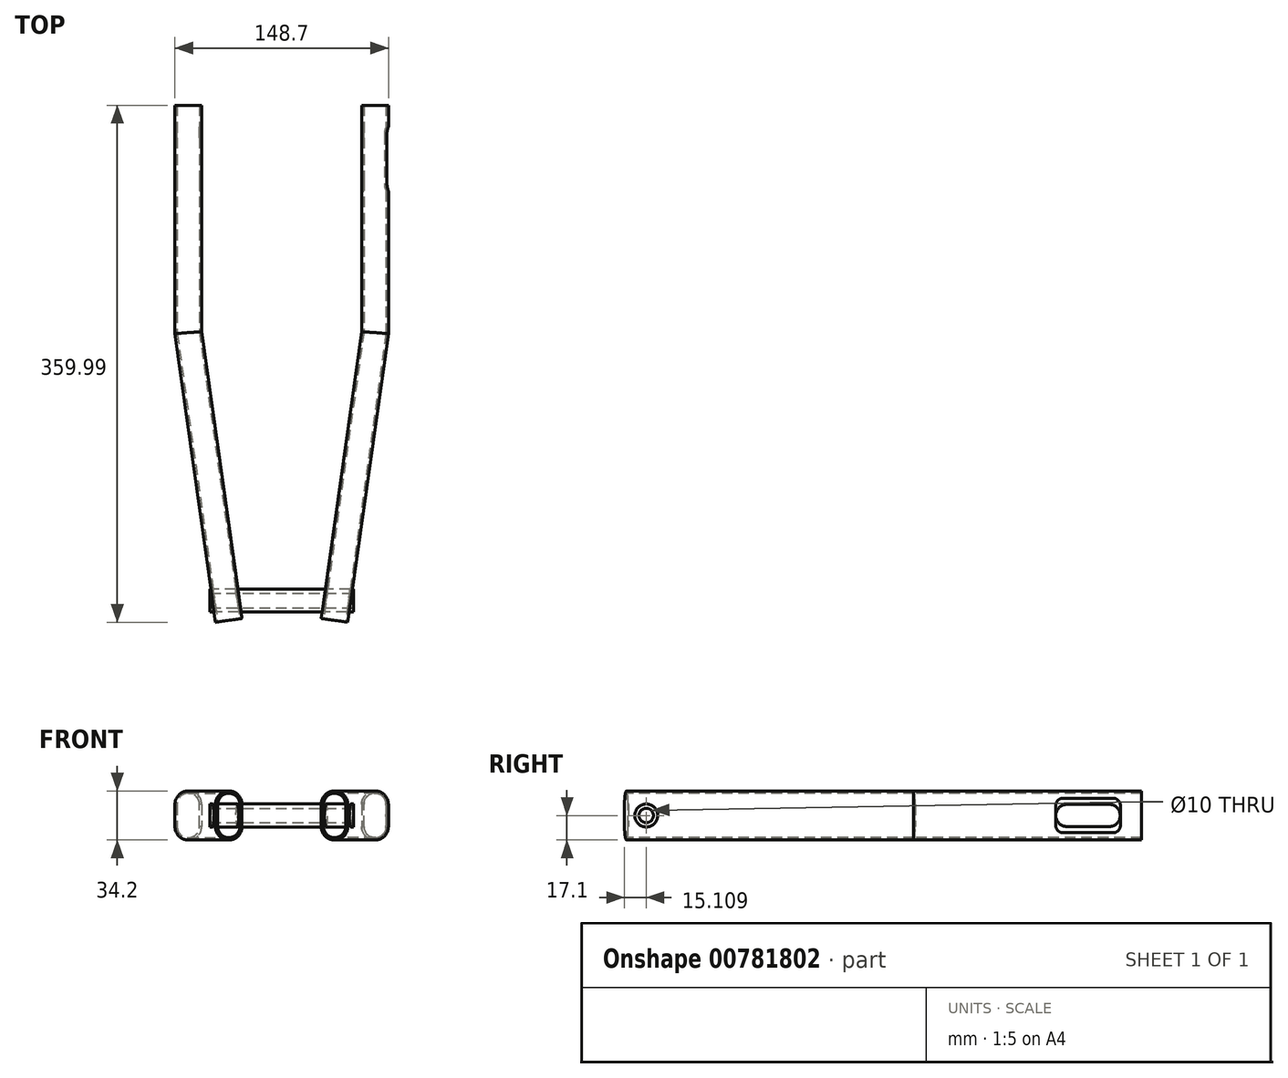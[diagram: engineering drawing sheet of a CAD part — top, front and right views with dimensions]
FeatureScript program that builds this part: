
annotation { "Feature Type Name" : "Feature", "Feature Type Description" : "" }
export const myFeature = defineFeature(function(context is Context, id is Id, definition is map)
    precondition{}
    {
        {
            var Q0;
            Q0=qCreatedBy(makeId("Front.planeOp"),FACE);
            var sketch = newSketch(context, id + "F0", { "sketchPlane" : qUnion([Q0])});
            skLineSegment(sketch, "E0.left", {"start": v(-57.25, -7.75) * mm, "end": v(-57.25, 7.75) * mm});
            skLineSegment(sketch, "E0.right", {"start": v(-72.75, -7.75) * mm, "end": v(-72.75, 7.75) * mm});
            skPoint(sketch, "E0.middle", {"position": v(-65, 0) * mm});
            skArc(sketch, "E1", {"start": v(-57.25, 7.75) * mm, "mid": v(-65, 15.5) * mm, "end": v(-72.75, 7.75) * mm});
            skArc(sketch, "E2", {"start": v(-72.75, -7.75) * mm, "mid": v(-65, -15.5) * mm, "end": v(-57.25, -7.75) * mm});
            skLineSegment(sketch, "E3", {"start": v(-74.35, 7.75) * mm, "end": v(-74.35, -7.75) * mm});
            skLineSegment(sketch, "E4", {"start": v(-55.65, 7.75) * mm, "end": v(-55.65, -7.75) * mm});
            skArc(sketch, "E5", {"start": v(-55.65, 7.75) * mm, "mid": v(-65, 17.1) * mm, "end": v(-74.35, 7.75) * mm});
            skArc(sketch, "E6", {"start": v(-74.35, -7.75) * mm, "mid": v(-65, -17.1) * mm, "end": v(-55.65, -7.75) * mm});
            skLineSegment(sketch, "E7", {"start": v(-65, 0) * mm, "end": v(0, 0) * mm});
            skSolve(sketch);
        }
        {
            var Q0;
            Q0=qCreatedBy(makeId("Top.planeOp"),FACE);
            var sketch = newSketch(context, id + "F1", { "sketchPlane" : qUnion([Q0])});
            skPoint(sketch, "E8.start.orphan", {"position": v(-65, 0) * mm});
            skLineSegment(sketch, "E9", {"start": v(-65, 0) * mm, "end": v(-65, -158.3) * mm});
            skLineSegment(sketch, "E10", {"start": v(-65, -158.3) * mm, "end": v(-36.84, -358.7) * mm});
            skSolve(sketch);
        }
        {
            var Q0;
            Q0 = qSketchRegion(id + "F0", true);
            var Q1;
            Q1=sQuery(id+"F1.wireOp",EDGE,"E9");
            var Q2;
            Q2=sQuery(id+"F1.wireOp",EDGE,"E10");
            sweep(context, id + "F2", {"profiles" : qUnion([Q0]), "path" : qUnion([Q1, Q2])});
        }
        {
            var Q0;
            Q0=makeQuery(id+"F2.opSweep","SWEPT_BODY",BODY,{"disambiguationData":[OSD([sQuery(id+"F0.wireOp",EDGE,"E0.left"),sQuery(id+"F0.wireOp",EDGE,"E0.right"),sQuery(id+"F0.wireOp",EDGE,"E1"),sQuery(id+"F0.wireOp",EDGE,"E2"),sQuery(id+"F0.wireOp",EDGE,"E3"),sQuery(id+"F0.wireOp",EDGE,"E4"),sQuery(id+"F0.wireOp",EDGE,"E5"),sQuery(id+"F0.wireOp",EDGE,"E6"),sQuery(id+"F1.wireOp",EDGE,"E10")])]});
            var Q1;
            Q1=qCreatedBy(makeId("Right.planeOp"),FACE);
            mirror(context, id + "F3", {"operationType" : NewBodyOperationType.ADD, "entities" : qUnion([Q0]), "mirrorPlane" : qUnion([Q1])});
        }
        {
            var Q0;
            Q0=makeQuery(id+"F3.opPattern","COPY",FACE,{"derivedFrom":makeQuery(id+"F2.opSweep","SWEPT_FACE",FACE,{"disambiguationData":[OSD([sQuery(id+"F0.wireOp",EDGE,"E3"),sQuery(id+"F1.wireOp",EDGE,"E9")])]}),"instanceName":"1"});
            var sketch = newSketch(context, id + "F4", { "sketchPlane" : qUnion([Q0])});
            skLineSegment(sketch, "E11.bottom", {"start": v(-22.54, -7.75) * mm, "end": v(-52.04, -7.75) * mm});
            skLineSegment(sketch, "E11.top", {"start": v(-22.54, 7.75) * mm, "end": v(-52.04, 7.75) * mm});
            skPoint(sketch, "E11.middle", {"position": v(-37.3, 0) * mm});
            skArc(sketch, "E12", {"start": v(-22.54, -7.75) * mm, "mid": v(-14.79, 0) * mm, "end": v(-22.54, 7.75) * mm});
            skArc(sketch, "E13", {"start": v(-52.04, 7.75) * mm, "mid": v(-59.8, 0) * mm, "end": v(-52.04, -7.75) * mm});
            skSolve(sketch);
        }
        {
            var Q0;
            Q0 = qSketchRegion(id + "F4", true);
            extrude(context, id + "F5", {"entities" : qUnion([Q0]), "operationType" : NewBodyOperationType.REMOVE, "oppositeDirection" : true, "depth" : 25 * mm, "offsetDistance" : 25 * mm});
        }
        {
            var Q0;
            Q0=makeQuery(id+"F2.opSweep","SWEPT_FACE",FACE,{"disambiguationData":[OSD([sQuery(id+"F0.wireOp",EDGE,"E3"),sQuery(id+"F1.wireOp",EDGE,"E9")])]});
            var sketch = newSketch(context, id + "F6", { "sketchPlane" : qUnion([Q0])});
            skLineSegment(sketch, "E14.bottom", {"start": v(52.04, -7.75) * mm, "end": v(22.54, -7.75) * mm});
            skLineSegment(sketch, "E14.top", {"start": v(52.04, 7.75) * mm, "end": v(22.54, 7.75) * mm});
            skPoint(sketch, "E14.middle", {"position": v(37.3, 0) * mm});
            skArc(sketch, "E15", {"start": v(52.04, -7.75) * mm, "mid": v(59.8, 0) * mm, "end": v(52.04, 7.75) * mm});
            skArc(sketch, "E16", {"start": v(22.54, 7.75) * mm, "mid": v(14.79, 0) * mm, "end": v(22.54, -7.75) * mm});
            skSolve(sketch);
        }
        {
            var Q0;
            Q0 = qSketchRegion(id + "F6", true);
            extrude(context, id + "F7", {"entities" : qUnion([Q0]), "operationType" : NewBodyOperationType.REMOVE, "oppositeDirection" : true, "depth" : 25 * mm, "offsetDistance" : 25 * mm});
        }
        {
            var Q0;
            {var subQ2=sQuery(id+"F1.wireOp",EDGE,"E9");var subQ4=sQuery(id+"F0.wireOp",EDGE,"E3");Q0=makeQuery(id+"F5.boolean.opBoolean","SPLIT",FACE,{"disambiguationData":[TD([makeQuery(id+"F5.opExtrude","SWEPT_FACE",FACE,{"disambiguationData":[OSD([sQuery(id+"F4.wireOp",EDGE,"E13")])]})])],"derivedFrom":makeQuery(id+"F3.opPattern","COPY",FACE,{"derivedFrom":makeQuery(id+"F2.opSweep","SWEPT_FACE",FACE,{"disambiguationData":[OSD([subQ4,subQ2])]}),"instanceName":"1"})});}
            cPlane(context, id + "F8", {"entities" : qUnion([Q0]), "cplaneType" : CPlaneType.OFFSET, "offset" : 25 * mm, "width" : 150 * mm, "height" : 150 * mm});
        }
        {
            var Q0;
            Q0=qCreatedBy(id+"F8.planeOp",FACE);
            var sketch = newSketch(context, id + "F9", { "sketchPlane" : qUnion([Q0])});
            skLineSegment(sketch, "E17.bottom", {"start": v(-19.76, -12) * mm, "end": v(-54.76, -12) * mm});
            skLineSegment(sketch, "E17.top", {"start": v(-19.76, 12) * mm, "end": v(-54.76, 12) * mm});
            skLineSegment(sketch, "E17.left", {"start": v(-14.76, -7) * mm, "end": v(-14.76, 7) * mm});
            skLineSegment(sketch, "E17.right", {"start": v(-59.76, -7) * mm, "end": v(-59.76, 7) * mm});
            skPoint(sketch, "E17.middle", {"position": v(-37.26, 0) * mm});
            skPoint(sketch, "E18.visualSharp", {"position": v(-59.76, 12) * mm});
            skArc(sketch, "E18.filletArc", {"start": v(-54.76, 12) * mm, "mid": v(-58.3, 10.54) * mm, "end": v(-59.76, 7) * mm});
            skPoint(sketch, "E19.visualSharp", {"position": v(-14.76, 12) * mm});
            skArc(sketch, "E19.filletArc", {"start": v(-14.76, 7) * mm, "mid": v(-16.22, 10.54) * mm, "end": v(-19.76, 12) * mm});
            skPoint(sketch, "E20.visualSharp", {"position": v(-14.76, -12) * mm});
            skArc(sketch, "E20.filletArc", {"start": v(-19.76, -12) * mm, "mid": v(-16.22, -10.54) * mm, "end": v(-14.76, -7) * mm});
            skPoint(sketch, "E21.visualSharp", {"position": v(-59.76, -12) * mm});
            skArc(sketch, "E21.filletArc", {"start": v(-59.76, -7) * mm, "mid": v(-58.3, -10.54) * mm, "end": v(-54.76, -12) * mm});
            skSolve(sketch);
        }
        {
            var Q0;
            Q0 = qSketchRegion(id + "F9", true);
            extrude(context, id + "F10", {"entities" : qUnion([Q0]), "operationType" : NewBodyOperationType.REMOVE, "oppositeDirection" : true, "depth" : 30 * mm, "offsetDistance" : 25 * mm});
        }
        {
            var Q0;
            Q0=makeQuery(id+"F3.opPattern","COPY",BODY,{"derivedFrom":makeQuery(id+"F2.opSweep","SWEPT_BODY",BODY,{"disambiguationData":[OSD([sQuery(id+"F0.wireOp",EDGE,"E0.left"),sQuery(id+"F0.wireOp",EDGE,"E0.right"),sQuery(id+"F0.wireOp",EDGE,"E1"),sQuery(id+"F0.wireOp",EDGE,"E2"),sQuery(id+"F0.wireOp",EDGE,"E3"),sQuery(id+"F0.wireOp",EDGE,"E4"),sQuery(id+"F0.wireOp",EDGE,"E5"),sQuery(id+"F0.wireOp",EDGE,"E6"),sQuery(id+"F1.wireOp",EDGE,"E10")])]}),"instanceName":"1"});
            var Q1;
            Q1=qCreatedBy(makeId("Right.planeOp"),FACE);
            mirror(context, id + "F11", {"operationType" : NewBodyOperationType.ADD, "entities" : qUnion([Q0]), "mirrorPlane" : qUnion([Q1])});
        }
        {
            var Q0;
            Q0=makeQuery(id+"F3.opPattern","COPY",BODY,{"derivedFrom":makeQuery(id+"F2.opSweep","SWEPT_BODY",BODY,{"disambiguationData":[OSD([sQuery(id+"F0.wireOp",EDGE,"E0.left"),sQuery(id+"F0.wireOp",EDGE,"E0.right"),sQuery(id+"F0.wireOp",EDGE,"E1"),sQuery(id+"F0.wireOp",EDGE,"E2"),sQuery(id+"F0.wireOp",EDGE,"E3"),sQuery(id+"F0.wireOp",EDGE,"E4"),sQuery(id+"F0.wireOp",EDGE,"E5"),sQuery(id+"F0.wireOp",EDGE,"E6"),sQuery(id+"F1.wireOp",EDGE,"E10")])]}),"instanceName":"1"});
            var Q1;
            Q1=qCreatedBy(makeId("Right.planeOp"),FACE);
            mirror(context, id + "F12", {"entities" : qUnion([Q0]), "mirrorPlane" : qUnion([Q1])});
        }
        {
            var Q0;
            Q0=qCreatedBy(makeId("Right.planeOp"),FACE);
            var sketch = newSketch(context, id + "F13", { "sketchPlane" : qUnion([Q0])});
            skCircle(sketch, "E22", {"center": v(-344.88, 0) * mm, "radius": 8 * mm});
            skSolve(sketch);
        }
        {
            var Q0;
            Q0=makeQuery(id+"F13.imprint","IMPRINT",FACE,{"disambiguationData":[TD([[makeQuery(id+"F13.imprint","IMPRINT",EDGE,{"derivedFrom":sQuery(id+"F13.wireOp",EDGE,"E22")}),1.0]])]});
            extrude(context, id + "F14", {"entities" : qUnion([Q0]), "operationType" : NewBodyOperationType.ADD, "endBound" : BoundingType.SYMMETRIC, "depth" : 100 * mm, "offsetDistance" : 25 * mm});
        }
        {
            var Q0;
            Q0=makeQuery(id+"F14.opExtrude","CAP_FACE",FACE,{"disambiguationData":[OSD([sQuery(id+"F13.wireOp",EDGE,"E22")])],"isStart":false});
            var sketch = newSketch(context, id + "F15", { "sketchPlane" : qUnion([Q0])});
            skCircle(sketch, "E23", {"center": v(-344.88, 0) * mm, "radius": 5 * mm});
            skSolve(sketch);
        }
        {
            var Q0;
            Q0=makeQuery(id+"F15.imprint","IMPRINT",FACE,{"disambiguationData":[TD([[makeQuery(id+"F15.imprint","IMPRINT",EDGE,{"derivedFrom":sQuery(id+"F15.wireOp",EDGE,"E23")}),1.0]])]});
            extrude(context, id + "F16", {"entities" : qUnion([Q0]), "operationType" : NewBodyOperationType.REMOVE, "oppositeDirection" : true, "depth" : 110 * mm, "offsetDistance" : 25 * mm});
        }
    });
